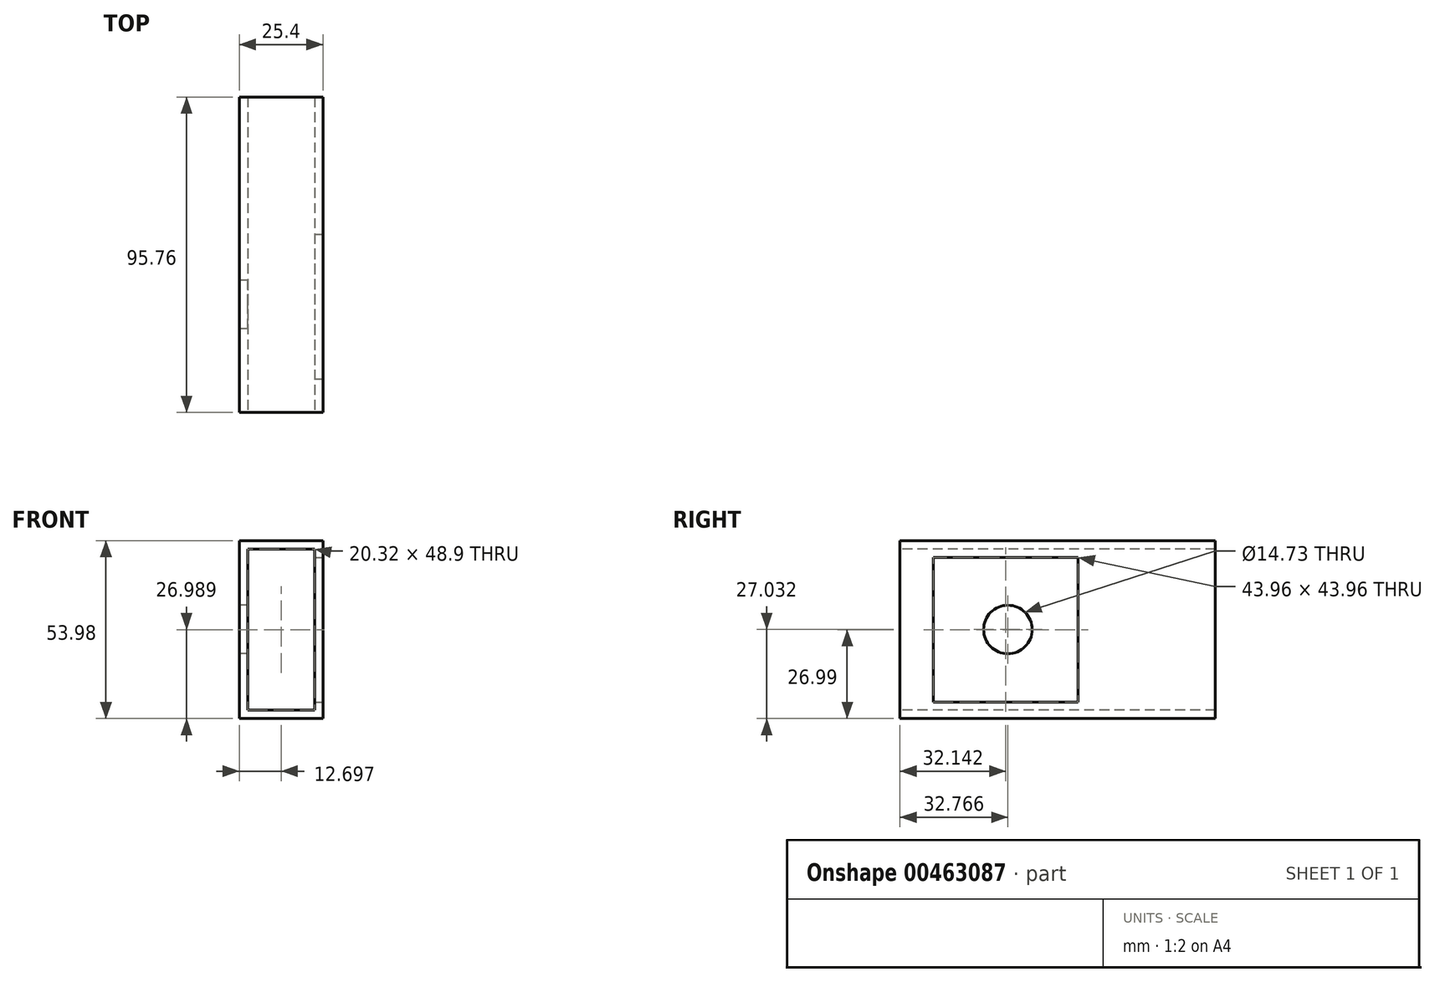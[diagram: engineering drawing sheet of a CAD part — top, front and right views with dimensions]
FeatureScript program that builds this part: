
annotation { "Feature Type Name" : "Feature", "Feature Type Description" : "" }
export const myFeature = defineFeature(function(context is Context, id is Id, definition is map)
    precondition{}
    {
        {
            var Q0;
            Q0=qCreatedBy(makeId("Front.planeOp"),FACE);
            var sketch = newSketch(context, id + "F0", { "sketchPlane" : qUnion([Q0])});
            skLineSegment(sketch, "E0.bottom", {"start": v(-69.82, -19.36) * mm, "end": v(-44.42, -19.36) * mm});
            skLineSegment(sketch, "E0.top", {"start": v(-69.82, -73.34) * mm, "end": v(-44.42, -73.34) * mm});
            skLineSegment(sketch, "E0.left", {"start": v(-69.82, -19.36) * mm, "end": v(-69.82, -73.34) * mm});
            skLineSegment(sketch, "E0.right", {"start": v(-44.42, -19.36) * mm, "end": v(-44.42, -73.34) * mm});
            skLineSegment(sketch, "E1.0", {"start": v(-67.28, -21.9) * mm, "end": v(-67.28, -70.8) * mm});
            skLineSegment(sketch, "E1.1", {"start": v(-67.28, -21.9) * mm, "end": v(-46.96, -21.9) * mm});
            skLineSegment(sketch, "E1.2", {"start": v(-46.96, -21.9) * mm, "end": v(-46.96, -70.8) * mm});
            skLineSegment(sketch, "E1.3", {"start": v(-67.28, -70.8) * mm, "end": v(-46.96, -70.8) * mm});
            skSolve(sketch);
        }
        {
            var Q0;
            Q0 = qSketchRegion(id + "F0", true);
            extrude(context, id + "F1", {"entities" : qUnion([Q0]), "oppositeDirection" : true, "depth" : 95.76 * mm});
        }
        {
            var Q0;
            Q0=makeQuery(id+"F1.opExtrude","SWEPT_FACE",FACE,{"disambiguationData":[OSD([sQuery(id+"F0.wireOp",EDGE,"E0.left")])]});
            var sketch = newSketch(context, id + "F2", { "sketchPlane" : qUnion([Q0])});
            skPoint(sketch, "E2", {"position": v(-32.77, -46.3) * mm});
            skPoint(sketch, "E2.positionSnap0", {"position": v(-32.77, -20.9) * mm});
            skPoint(sketch, "E2.positionSnap1", {"position": v(-106.36, -46.3) * mm});
            skCircle(sketch, "E3", {"center": v(-32.77, -46.3) * mm, "radius": 7.37 * mm});
            skSolve(sketch);
        }
        {
            var Q0;
            Q0=makeQuery(id+"F2.imprint","IMPRINT",FACE,{"disambiguationData":[TD([[makeQuery(id+"F2.imprint","IMPRINT",EDGE,{"derivedFrom":sQuery(id+"F2.wireOp",EDGE,"E3")}),1.0]])]});
            extrude(context, id + "F3", {"entities" : qUnion([Q0]), "operationType" : NewBodyOperationType.REMOVE, "oppositeDirection" : true, "depth" : 50.3 * mm});
        }
        {
            var Q0;
            Q0=makeQuery(id+"F1.opExtrude","SWEPT_FACE",FACE,{"disambiguationData":[OSD([sQuery(id+"F0.wireOp",EDGE,"E0.right")])]});
            var sketch = newSketch(context, id + "F4", { "sketchPlane" : qUnion([Q0])});
            skLineSegment(sketch, "E4.bottom", {"start": v(10.16, -24.37) * mm, "end": v(54.12, -24.37) * mm});
            skLineSegment(sketch, "E4.top", {"start": v(10.16, -68.33) * mm, "end": v(54.12, -68.33) * mm});
            skLineSegment(sketch, "E4.left", {"start": v(10.16, -24.37) * mm, "end": v(10.16, -68.33) * mm});
            skLineSegment(sketch, "E4.right", {"start": v(54.12, -24.37) * mm, "end": v(54.12, -68.33) * mm});
            skPoint(sketch, "E5.endSnap0", {"position": v(0, -46.35) * mm});
            skSolve(sketch);
        }
        {
            var Q0;
            Q0=makeQuery(id+"F4.imprint","IMPRINT",FACE,{"disambiguationData":[TD([[makeQuery(id+"F4.imprint","IMPRINT",EDGE,{"derivedFrom":sQuery(id+"F4.wireOp",EDGE,"E4.bottom")}),-1.0]])]});
            extrude(context, id + "F5", {"entities" : qUnion([Q0]), "operationType" : NewBodyOperationType.REMOVE, "oppositeDirection" : true, "depth" : 9.9 * mm});
        }
    });
